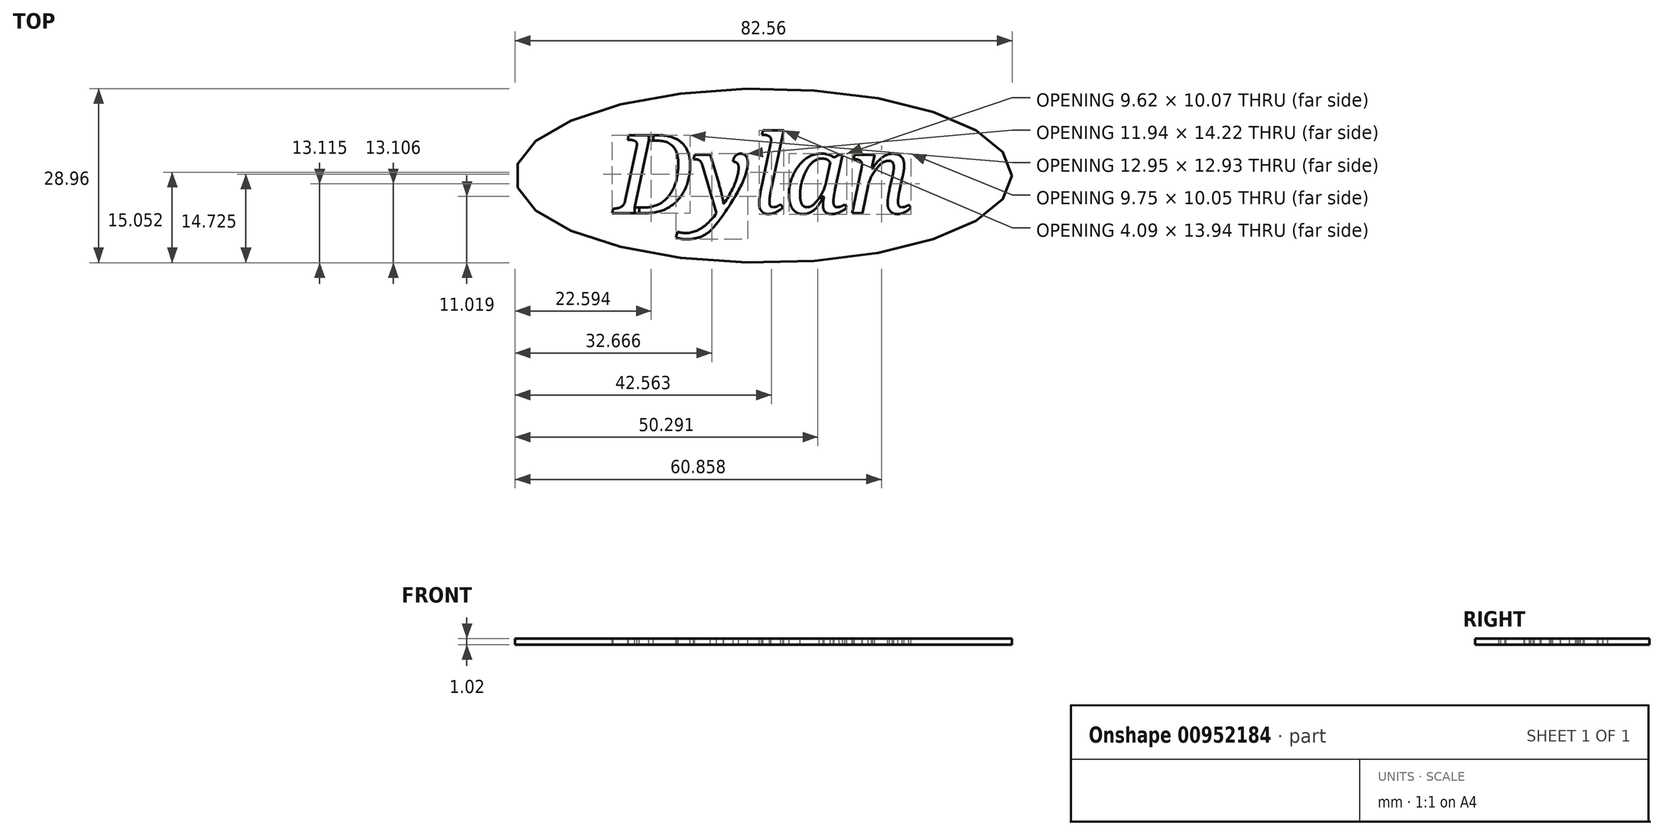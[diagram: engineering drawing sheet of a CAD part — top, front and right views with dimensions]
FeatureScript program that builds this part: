
annotation { "Feature Type Name" : "Feature", "Feature Type Description" : "" }
export const myFeature = defineFeature(function(context is Context, id is Id, definition is map)
    precondition{}
    {
        {
            var Q0;
            Q0=qCreatedBy(makeId("Top.planeOp"),FACE);
            var sketch = newSketch(context, id + "F0", { "sketchPlane" : qUnion([Q0])});
            skEllipse(sketch, "E0", {"center": v(0, 0) * mm, "majorRadius": 41.28 * mm, "minorRadius": 14.48 * mm, "majorAxis": v(1, 0)});
            skSolve(sketch);
        }
        {
            var Q0;
            Q0=makeQuery(id+"F0.imprint","IMPRINT",FACE,{"disambiguationData":[TD([[makeQuery(id+"F0.imprint","IMPRINT",EDGE,{"derivedFrom":sQuery(id+"F0.wireOp",EDGE,"E0")}),1.0]])]});
            extrude(context, id + "F1", {"entities" : qUnion([Q0]), "depth" : 1.02 * mm, "offsetDistance" : 25.4 * mm});
        }
        {
            var Q0;
            Q0=makeQuery(id+"F1.opExtrude","CAP_FACE",FACE,{"disambiguationData":[OSD([sQuery(id+"F0.wireOp",EDGE,"E0")])],"isStart":false});
            var sketch = newSketch(context, id + "F2", { "sketchPlane" : qUnion([Q0])});
            skText(sketch, "E1", { "text": "Dylan", "fontName": "NotoSerif-Italic.ttf"});
            const initialGuessF2  = {"E1": [-0.02478, -0.00622, 1, 0, 0.01304]};
            skSetInitialGuess(sketch, initialGuessF2);
            skSolve(sketch);
        }
        {
            var Q0;
            Q0=qSketchRegion(id+"F2",true);
            extrude(context, id + "F3", {"entities" : qUnion([Q0]), "operationType" : NewBodyOperationType.REMOVE, "endBound" : BoundingType.THROUGH_ALL, "oppositeDirection" : true, "depth" : 25.4 * mm, "offsetDistance" : 25.4 * mm});
        }
        {
            var Q0;
            Q0=makeQuery(id+"F3.boolean.opBoolean","SPLIT",FACE,{"disambiguationData":[TD([makeQuery(id+"F3.opExtrude","SWEPT_FACE",FACE,{"disambiguationData":[OSD([sQuery(id+"F2.wireOp",EDGE,"E1.sketch_text.stroke-14")])]})])],"derivedFrom":makeQuery(id+"F1.opExtrude","CAP_FACE",FACE,{"disambiguationData":[OSD([sQuery(id+"F0.wireOp",EDGE,"E0")])],"isStart":false})});
            var sketch = newSketch(context, id + "F4", { "sketchPlane" : qUnion([Q0])});
            skPoint(sketch, "E2.oppositeSnap0", {"position": v(-18.34, 5.81) * mm});
            skLineSegment(sketch, "E2.bottom", {"start": v(-19.06, 5.81) * mm, "end": v(-18.34, 5.81) * mm});
            skLineSegment(sketch, "E2.top", {"start": v(-19.06, 6.74) * mm, "end": v(-18.34, 6.74) * mm});
            skLineSegment(sketch, "E2.left", {"start": v(-19.06, 5.81) * mm, "end": v(-19.06, 6.74) * mm});
            skLineSegment(sketch, "E2.right", {"start": v(-18.34, 5.81) * mm, "end": v(-18.34, 6.74) * mm});
            skPoint(sketch, "E3.oppositeSnap0", {"position": v(-20.64, -5.3) * mm});
            skLineSegment(sketch, "E3.bottom", {"start": v(-21.43, -5.3) * mm, "end": v(-20.64, -5.3) * mm});
            skLineSegment(sketch, "E3.top", {"start": v(-21.43, -6.23) * mm, "end": v(-20.64, -6.23) * mm});
            skLineSegment(sketch, "E3.left", {"start": v(-21.43, -5.3) * mm, "end": v(-21.43, -6.23) * mm});
            skLineSegment(sketch, "E3.right", {"start": v(-20.64, -5.3) * mm, "end": v(-20.64, -6.23) * mm});
            skLineSegment(sketch, "E4.bottom", {"start": v(9.94, -3.7) * mm, "end": v(9.23, -3.7) * mm});
            skLineSegment(sketch, "E4.top", {"start": v(9.94, -3.49) * mm, "end": v(9.23, -3.49) * mm});
            skLineSegment(sketch, "E4.left", {"start": v(9.94, -3.7) * mm, "end": v(9.94, -3.49) * mm});
            skLineSegment(sketch, "E4.right", {"start": v(9.23, -3.7) * mm, "end": v(9.23, -3.49) * mm});
            skSolve(sketch);
        }
        {
            var Q0;
            Q0=qSketchRegion(id+"F4",true);
            var Q1;
            {var subQ0=sQuery(id+"F0.wireOp",EDGE,"E0");Q1=makeQuery(id+"F3.boolean.opBoolean","SPLIT",FACE,{"disambiguationData":[TD([makeQuery(id+"F1.opExtrude","SWEPT_FACE",FACE,{"disambiguationData":[OSD([subQ0])]})])],"derivedFrom":makeQuery(id+"F1.opExtrude","CAP_FACE",FACE,{"disambiguationData":[OSD([subQ0])],"isStart":true})});}
            extrude(context, id + "F5", {"entities" : qUnion([Q0]), "endBound" : BoundingType.UP_TO_SURFACE, "oppositeDirection" : true, "depth" : 25.4 * mm, "endBoundEntityFace" : qUnion([Q1]), "offsetDistance" : 25.4 * mm});
        }
    });
